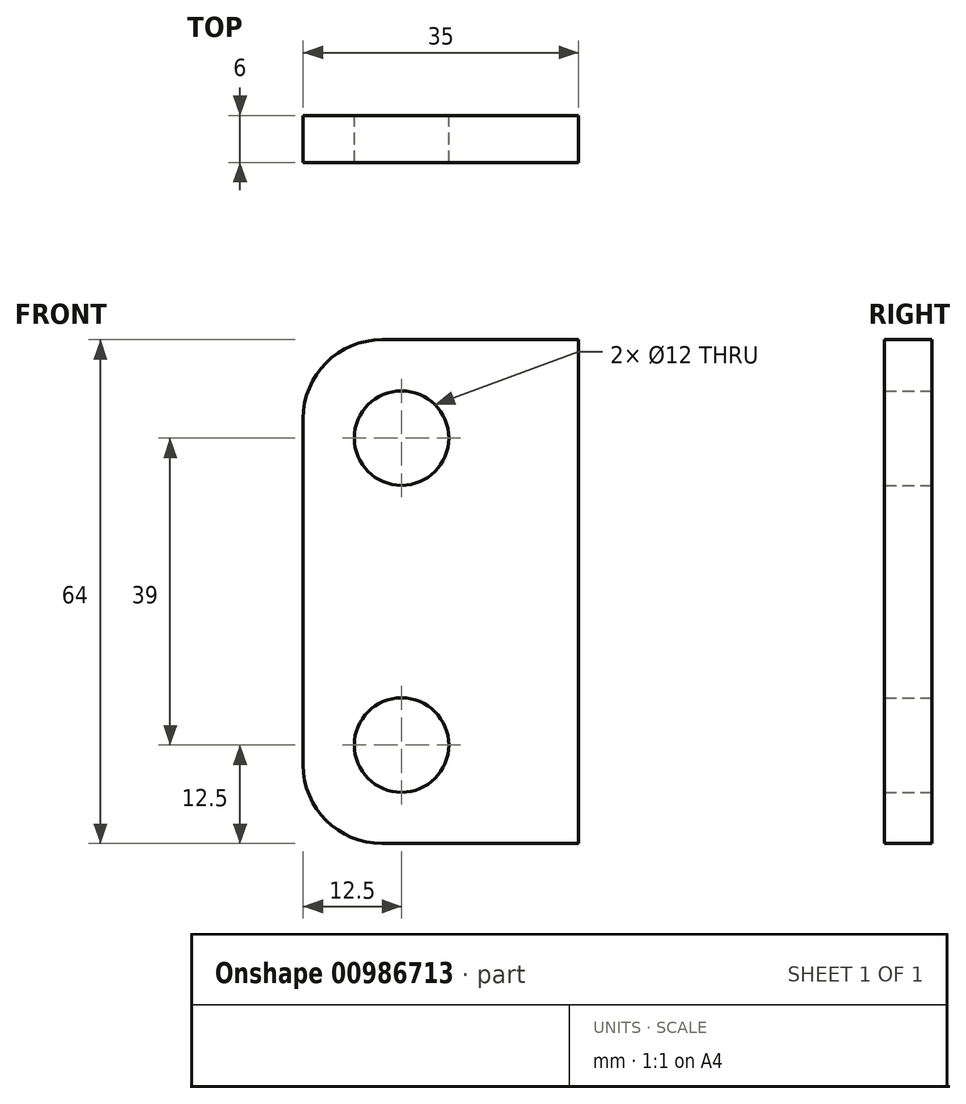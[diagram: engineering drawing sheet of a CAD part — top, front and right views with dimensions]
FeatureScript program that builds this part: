
annotation { "Feature Type Name" : "Feature", "Feature Type Description" : "" }
export const myFeature = defineFeature(function(context is Context, id is Id, definition is map)
    precondition{}
    {
        {
            var Q0;
            Q0=qCreatedBy(makeId("Front.planeOp"),FACE);
            var sketch = newSketch(context, id + "F0", { "sketchPlane" : qUnion([Q0])});
            skLineSegment(sketch, "E0.bottom", {"start": v(-7.5, -32) * mm, "end": v(17.5, -32) * mm});
            skLineSegment(sketch, "E0.top", {"start": v(-7.5, 32) * mm, "end": v(17.5, 32) * mm});
            skLineSegment(sketch, "E0.left", {"start": v(-17.5, -22) * mm, "end": v(-17.5, 22) * mm});
            skLineSegment(sketch, "E0.right", {"start": v(17.5, -32) * mm, "end": v(17.5, 32) * mm});
            skPoint(sketch, "E0.middle", {"position": v(0, 0) * mm});
            skLineSegment(sketch, "E1", {"start": v(-17.5, 32) * mm, "end": v(-17.5, 19.5) * mm, "construction": true});
            skLineSegment(sketch, "E2", {"start": v(-17.5, 19.5) * mm, "end": v(-5, 19.5) * mm, "construction": true});
            skLineSegment(sketch, "E3", {"start": v(-5, 19.5) * mm, "end": v(-5, -19.5) * mm, "construction": true});
            skCircle(sketch, "E4", {"center": v(-5, 19.5) * mm, "radius": 6 * mm});
            skCircle(sketch, "E5", {"center": v(-5, -19.5) * mm, "radius": 6 * mm});
            skPoint(sketch, "E6.visualSharp", {"position": v(-17.5, 32) * mm});
            skArc(sketch, "E6.filletArc", {"start": v(-7.5, 32) * mm, "mid": v(-14.57, 29.07) * mm, "end": v(-17.5, 22) * mm});
            skPoint(sketch, "E7.visualSharp", {"position": v(-17.5, -32) * mm});
            skArc(sketch, "E7.filletArc", {"start": v(-17.5, -22) * mm, "mid": v(-14.57, -29.07) * mm, "end": v(-7.5, -32) * mm});
            skSolve(sketch);
        }
        {
            var Q0;
            Q0=makeQuery(id+"F0.imprint","IMPRINT",FACE,{"disambiguationData":[TD([[makeQuery(id+"F0.imprint","IMPRINT",EDGE,{"derivedFrom":sQuery(id+"F0.wireOp",EDGE,"E0.bottom")}),1.0]])]});
            extrude(context, id + "F1", {"entities" : qUnion([Q0]), "depth" : 6 * mm, "offsetDistance" : 25 * mm});
        }
    });
